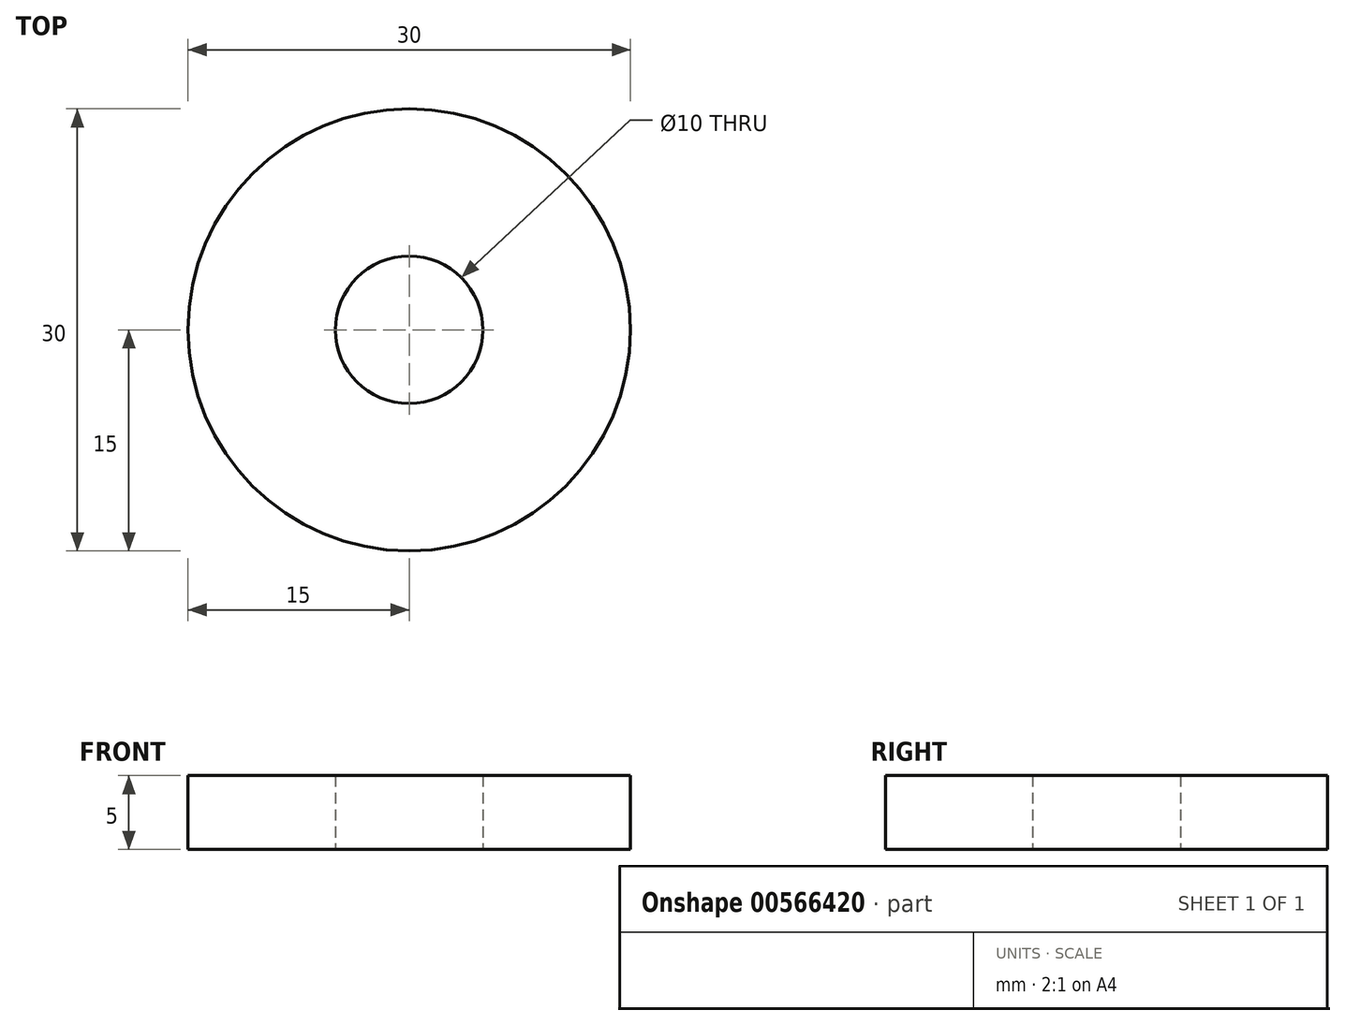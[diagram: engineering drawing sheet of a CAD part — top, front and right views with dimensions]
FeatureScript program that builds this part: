
annotation { "Feature Type Name" : "Feature", "Feature Type Description" : "" }
export const myFeature = defineFeature(function(context is Context, id is Id, definition is map)
    precondition{}
    {
        {
            var Q0;
            Q0=qCreatedBy(makeId("Top.planeOp"),FACE);
            var sketch = newSketch(context, id + "F0", { "sketchPlane" : qUnion([Q0])});
            skCircle(sketch, "E0", {"center": v(0, 0) * mm, "radius": 15 * mm});
            skCircle(sketch, "E1", {"center": v(0, 0) * mm, "radius": 5 * mm});
            skSolve(sketch);
        }
        {
            var Q0;
            Q0 = qSketchRegion(id + "F0", true);
            extrude(context, id + "F1", {"entities" : qUnion([Q0]), "endBound" : BoundingType.SYMMETRIC, "depth" : 5 * mm, "offsetDistance" : 25 * mm});
        }
    });
